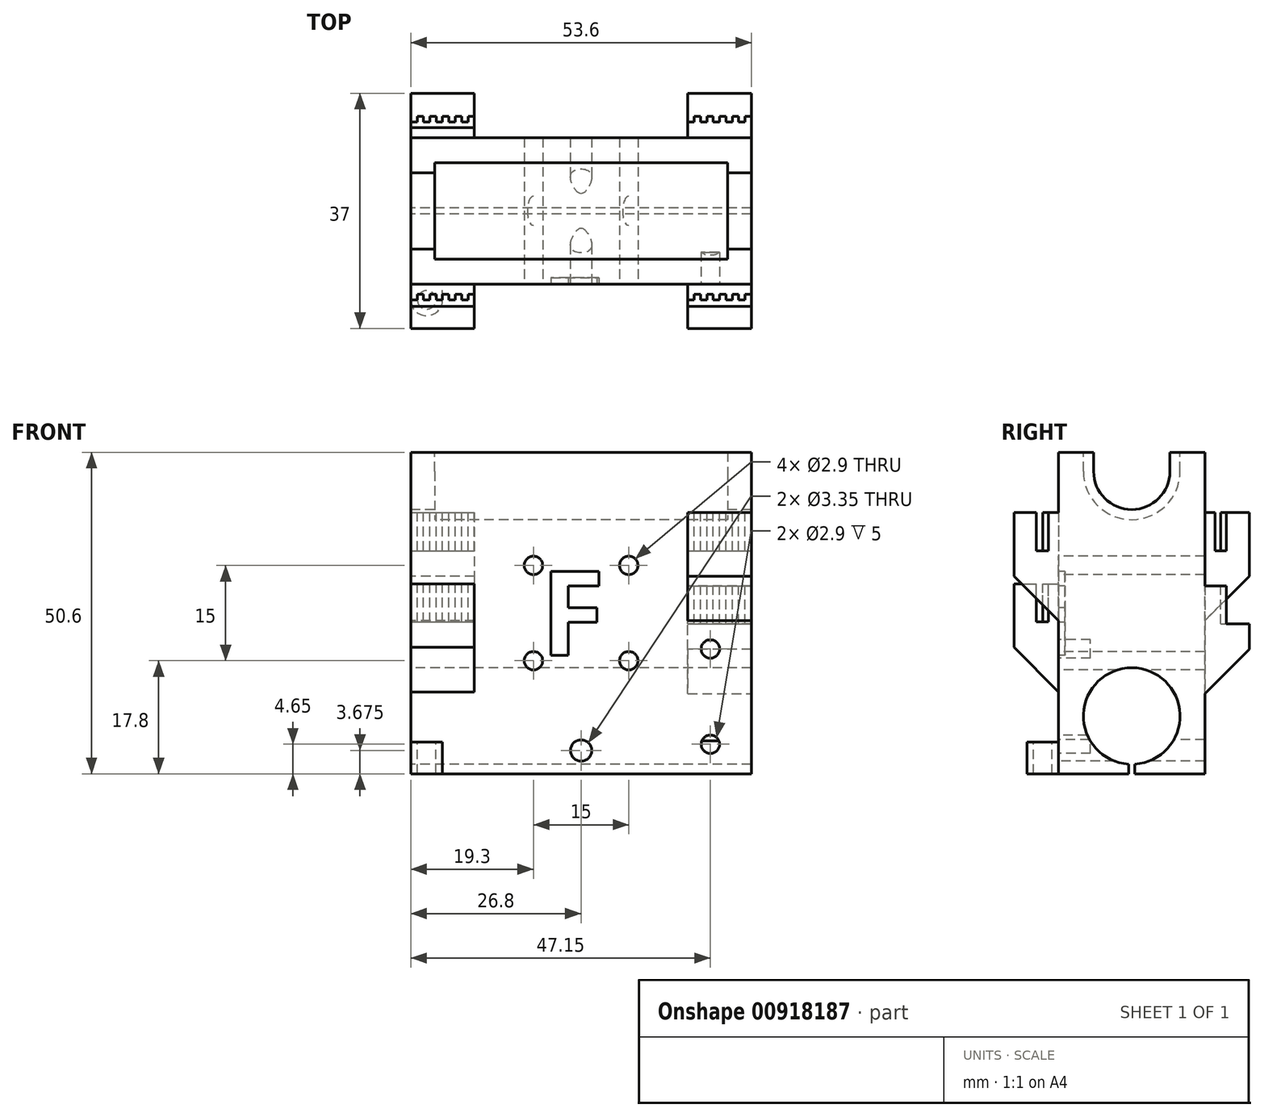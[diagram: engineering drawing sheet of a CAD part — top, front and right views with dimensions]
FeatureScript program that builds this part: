
annotation { "Feature Type Name" : "Feature", "Feature Type Description" : "" }
export const myFeature = defineFeature(function(context is Context, id is Id, definition is map)
    precondition{}
    {
        {
            assignVariable(context, id + "F0", {"name" : "LM8LUU", "anyValue" : 1.8});
        }
        {
            var Q0;
            Q0=qCreatedBy(makeId("Top.planeOp"),FACE);
            var sketch = newSketch(context, id + "F1", { "sketchPlane" : qUnion([Q0])});
            skLineSegment(sketch, "E0.bottom", {"start": v(0, 0) * mm, "end": v(53.6, 0) * mm});
            skLineSegment(sketch, "E0.top", {"start": v(0, 23) * mm, "end": v(53.6, 23) * mm});
            skLineSegment(sketch, "E0.left", {"start": v(0, 0) * mm, "end": v(0, 23) * mm});
            skLineSegment(sketch, "E0.right", {"start": v(53.6, 0) * mm, "end": v(53.6, 23) * mm});
            skSolve(sketch);
        }
        {
            var Q0;
            Q0=qSketchRegion(id+"F1",true);
            extrude(context, id + "F2", {"entities" : qUnion([Q0]), "depth" : 50.6 * mm});
        }
        {
            var Q0;
            Q0=makeQuery(id+"F2.opExtrude","SWEPT_FACE",FACE,{"disambiguationData":[OSD([sQuery(id+"F1.wireOp",EDGE,"E0.left")])]});
            var sketch = newSketch(context, id + "F3", { "sketchPlane" : qUnion([Q0])});
            skCircle(sketch, "E1", {"center": v(-11.5, 9.1) * mm, "radius": 7.6 * mm});
            skCircle(sketch, "E2", {"center": v(-11.5, 47.6) * mm, "radius": 6 * mm});
            skLineSegment(sketch, "E3", {"start": v(-23, 47.6) * mm, "end": v(0, 47.6) * mm, "construction": true});
            skLineSegment(sketch, "E4", {"start": v(-17.5, 50.6) * mm, "end": v(-17.5, 47.6) * mm});
            skLineSegment(sketch, "E5", {"start": v(-5.5, 50.6) * mm, "end": v(-5.5, 47.6) * mm});
            skLineSegment(sketch, "E6", {"start": v(-23, 9.1) * mm, "end": v(0, 9.1) * mm, "construction": true});
            skLineSegment(sketch, "E7", {"start": v(-11.5, 9.1) * mm, "end": v(-11.5, 0) * mm, "construction": true});
            skLineSegment(sketch, "E8", {"start": v(-11.5, 0) * mm, "end": v(-12, 0) * mm});
            skLineSegment(sketch, "E9", {"start": v(-12, 0) * mm, "end": v(-12, 1.52) * mm});
            skLineSegment(sketch, "E10", {"start": v(-12, 1.52) * mm, "end": v(-11, 1.52) * mm});
            skLineSegment(sketch, "E11", {"start": v(-11, 1.52) * mm, "end": v(-11, 0) * mm});
            skLineSegment(sketch, "E12", {"start": v(-11, 0) * mm, "end": v(-11.5, 0) * mm});
            skLineSegment(sketch, "E13", {"start": v(-11.5, 15.6) * mm, "end": v(-11.5, 16.7) * mm});
            skLineSegment(sketch, "E14", {"start": v(-11.5, 15.6) * mm, "end": v(-7, 15.22) * mm});
            skLineSegment(sketch, "E15", {"start": v(-11.5, 15.6) * mm, "end": v(-16, 15.22) * mm});
            skCircle(sketch, "E16", {"center": v(-11.5, 47.6) * mm, "radius": 7.6 * mm});
            skLineSegment(sketch, "E17", {"start": v(-3.9, 47.6) * mm, "end": v(-3.9, 50.6) * mm});
            skLineSegment(sketch, "E18", {"start": v(-19.1, 47.6) * mm, "end": v(-19.1, 50.6) * mm});
            skSolve(sketch);
        }
        {
            var Q0;
            {var subQ0=sQuery(id+"F3.wireOp",EDGE,"E14");var subQ1=sQuery(id+"F3.wireOp",EDGE,"E1");var subQ3=makeQuery(id+"F3.imprint","INTERSECT",VERTEX,{"disambiguationData":[OD(0.0)],"derivedFrom":[subQ1,subQ0]});Q0=makeQuery(id+"F3.imprint","IMPRINT",FACE,{"disambiguationData":[TD([[makeQuery(id+"F3.imprint","IMPRINT",EDGE,{"disambiguationData":[TD([[subQ3,-1.0]])],"derivedFrom":subQ1}),1.0]])]});}
            var Q1;
            {var subQ0=sQuery(id+"F3.wireOp",EDGE,"E15");var subQ1=sQuery(id+"F3.wireOp",EDGE,"E1");var subQ3=makeQuery(id+"F3.imprint","INTERSECT",VERTEX,{"disambiguationData":[OD(0.0)],"derivedFrom":[subQ1,subQ0]});Q1=makeQuery(id+"F3.imprint","IMPRINT",FACE,{"disambiguationData":[TD([[makeQuery(id+"F3.imprint","IMPRINT",EDGE,{"disambiguationData":[TD([[subQ3,1.0]])],"derivedFrom":subQ1}),1.0]])]});}
            var Q2;
            Q2=makeQuery(id+"F3.imprint","IMPRINT",FACE,{"disambiguationData":[TD([[makeQuery(id+"F3.imprint","IMPRINT",EDGE,{"derivedFrom":sQuery(id+"F3.wireOp",EDGE,"E8")}),-1.0]])]});
            var Q3;
            {var subQ0=sQuery(id+"F3.wireOp",EDGE,"E10");Q3=makeQuery(id+"F3.imprint","IMPRINT",FACE,{"disambiguationData":[TD([[makeQuery(id+"F3.imprint","IMPRINT",EDGE,{"derivedFrom":subQ0}),-1.0]])]});}
            var Q4;
            {var subQ3=sQuery(id+"F3.wireOp",EDGE,"E13");Q4=makeQuery(id+"F3.imprint","IMPRINT",FACE,{"disambiguationData":[TD([[makeQuery(id+"F3.imprint","IMPRINT",EDGE,{"derivedFrom":subQ3}),-1.0]])]});}
            var Q5;
            {var subQ3=sQuery(id+"F3.wireOp",EDGE,"E13");Q5=makeQuery(id+"F3.imprint","IMPRINT",FACE,{"disambiguationData":[TD([[makeQuery(id+"F3.imprint","IMPRINT",EDGE,{"derivedFrom":subQ3}),1.0]])]});}
            var Q6;
            {var subQ7=sQuery(id+"F3.wireOp",EDGE,"E10");Q6=makeQuery(id+"F3.imprint","IMPRINT",FACE,{"disambiguationData":[TD([[makeQuery(id+"F3.imprint","IMPRINT",EDGE,{"derivedFrom":subQ7}),1.0]])]});}
            var Q7;
            {var subQ3=sQuery(id+"F3.wireOp",EDGE,"E5");Q7=makeQuery(id+"F3.imprint","IMPRINT",FACE,{"disambiguationData":[TD([[makeQuery(id+"F3.imprint","IMPRINT",EDGE,{"derivedFrom":subQ3}),-1.0]])]});}
            var Q8;
            {var subQ0=sQuery(id+"F3.wireOp",EDGE,"E4");Q8=makeQuery(id+"F3.imprint","IMPRINT",FACE,{"disambiguationData":[TD([[makeQuery(id+"F3.imprint","IMPRINT",EDGE,{"derivedFrom":subQ0}),1.0]])]});}
            var Q9;
            {var subQ0=sQuery(id+"F3.wireOp",EDGE,"E4");Q9=makeQuery(id+"F3.imprint","IMPRINT",FACE,{"disambiguationData":[TD([[makeQuery(id+"F3.imprint","IMPRINT",EDGE,{"derivedFrom":subQ0}),1.0]])]});}
            var Q10;
            {var subQ3=sQuery(id+"F3.wireOp",EDGE,"E5");Q10=makeQuery(id+"F3.imprint","IMPRINT",FACE,{"disambiguationData":[TD([[makeQuery(id+"F3.imprint","IMPRINT",EDGE,{"derivedFrom":subQ3}),-1.0]])]});}
            var Q11;
            {var subQ1=sQuery(id+"F3.wireOp",EDGE,"E2");var subQ4=makeQuery(id+"F3.imprint","INTERSECT",VERTEX,{"derivedFrom":[subQ1,sQuery(id+"F3.wireOp",EDGE,"E5")]});Q11=makeQuery(id+"F3.imprint","IMPRINT",FACE,{"disambiguationData":[TD([[makeQuery(id+"F3.imprint","IMPRINT",EDGE,{"disambiguationData":[TD([[subQ4,-1.0]])],"derivedFrom":subQ1}),1.0]])]});}
            extrude(context, id + "F4", {"entities" : qUnion([Q0, Q1, Q2, Q3, Q4, Q5, Q6, Q7, Q8, Q9, Q10, Q11]), "operationType" : NewBodyOperationType.REMOVE, "endBound" : BoundingType.THROUGH_ALL, "oppositeDirection" : true, "depth" : 25 * mm});
        }
        {
            var Q0;
            {var subQ3=sQuery(id+"F3.wireOp",EDGE,"E4");Q0=makeQuery(id+"F3.imprint","IMPRINT",FACE,{"disambiguationData":[TD([[makeQuery(id+"F3.imprint","IMPRINT",EDGE,{"derivedFrom":subQ3}),-1.0]])]});}
            var Q1;
            {var subQ3=sQuery(id+"F3.wireOp",EDGE,"E18");Q1=makeQuery(id+"F3.imprint","IMPRINT",FACE,{"disambiguationData":[TD([[makeQuery(id+"F3.imprint","IMPRINT",EDGE,{"derivedFrom":subQ3}),-1.0]])]});}
            var Q2;
            {var subQ3=sQuery(id+"F3.wireOp",EDGE,"E17");Q2=makeQuery(id+"F3.imprint","IMPRINT",FACE,{"disambiguationData":[TD([[makeQuery(id+"F3.imprint","IMPRINT",EDGE,{"derivedFrom":subQ3}),1.0]])]});}
            extrude(context, id + "F5", {"entities" : qUnion([Q0, Q1, Q2]), "operationType" : NewBodyOperationType.REMOVE, "oppositeDirection" : true, "depth" : (46.25 + getVariable(context, 'LM8LUU') * 2) * mm});
        }
        {
            var Q0;
            {var subQ3=sQuery(id+"F3.wireOp",EDGE,"E4");Q0=makeQuery(id+"F3.imprint","IMPRINT",FACE,{"disambiguationData":[TD([[makeQuery(id+"F3.imprint","IMPRINT",EDGE,{"derivedFrom":subQ3}),-1.0]])]});}
            var Q1;
            {var subQ3=sQuery(id+"F3.wireOp",EDGE,"E18");Q1=makeQuery(id+"F3.imprint","IMPRINT",FACE,{"disambiguationData":[TD([[makeQuery(id+"F3.imprint","IMPRINT",EDGE,{"derivedFrom":subQ3}),-1.0]])]});}
            var Q2;
            {var subQ3=sQuery(id+"F3.wireOp",EDGE,"E17");Q2=makeQuery(id+"F3.imprint","IMPRINT",FACE,{"disambiguationData":[TD([[makeQuery(id+"F3.imprint","IMPRINT",EDGE,{"derivedFrom":subQ3}),1.0]])]});}
            extrude(context, id + "F6", {"entities" : qUnion([Q0, Q1, Q2]), "operationType" : NewBodyOperationType.ADD, "oppositeDirection" : true, "depth" : (26.75 - getVariable(context, 'LM8LUU')) * mm});
        }
        {
            var Q0;
            {var subQ3=sQuery(id+"F3.wireOp",EDGE,"E4");Q0=makeQuery(id+"F3.imprint","IMPRINT",FACE,{"disambiguationData":[TD([[makeQuery(id+"F3.imprint","IMPRINT",EDGE,{"derivedFrom":subQ3}),-1.0]])]});}
            var Q1;
            {var subQ3=sQuery(id+"F3.wireOp",EDGE,"E18");Q1=makeQuery(id+"F3.imprint","IMPRINT",FACE,{"disambiguationData":[TD([[makeQuery(id+"F3.imprint","IMPRINT",EDGE,{"derivedFrom":subQ3}),-1.0]])]});}
            var Q2;
            {var subQ3=sQuery(id+"F3.wireOp",EDGE,"E17");Q2=makeQuery(id+"F3.imprint","IMPRINT",FACE,{"disambiguationData":[TD([[makeQuery(id+"F3.imprint","IMPRINT",EDGE,{"derivedFrom":subQ3}),1.0]])]});}
            extrude(context, id + "F7", {"entities" : qUnion([Q0, Q1, Q2]), "operationType" : NewBodyOperationType.REMOVE, "oppositeDirection" : true, "depth" : (23.25 + getVariable(context, 'LM8LUU')) * mm});
        }
        {
            var Q0;
            {var subQ3=sQuery(id+"F3.wireOp",EDGE,"E4");Q0=makeQuery(id+"F3.imprint","IMPRINT",FACE,{"disambiguationData":[TD([[makeQuery(id+"F3.imprint","IMPRINT",EDGE,{"derivedFrom":subQ3}),-1.0]])]});}
            var Q1;
            {var subQ3=sQuery(id+"F3.wireOp",EDGE,"E18");Q1=makeQuery(id+"F3.imprint","IMPRINT",FACE,{"disambiguationData":[TD([[makeQuery(id+"F3.imprint","IMPRINT",EDGE,{"derivedFrom":subQ3}),-1.0]])]});}
            var Q2;
            {var subQ3=sQuery(id+"F3.wireOp",EDGE,"E17");Q2=makeQuery(id+"F3.imprint","IMPRINT",FACE,{"disambiguationData":[TD([[makeQuery(id+"F3.imprint","IMPRINT",EDGE,{"derivedFrom":subQ3}),1.0]])]});}
            extrude(context, id + "F8", {"entities" : qUnion([Q0, Q1, Q2]), "operationType" : NewBodyOperationType.ADD, "oppositeDirection" : true, "depth" : 3.75 * mm});
        }
        {
            var Q0;
            Q0=makeQuery(id+"F2.opExtrude","SWEPT_FACE",FACE,{"disambiguationData":[OSD([sQuery(id+"F1.wireOp",EDGE,"E0.bottom")])]});
            var sketch = newSketch(context, id + "F9", { "sketchPlane" : qUnion([Q0])});
            skLineSegment(sketch, "E19.bottom", {"start": v(0, 29.9) * mm, "end": v(10, 29.9) * mm});
            skLineSegment(sketch, "E19.top", {"start": v(0, 9.9) * mm, "end": v(10, 9.9) * mm});
            skLineSegment(sketch, "E19.left", {"start": v(0, 29.9) * mm, "end": v(0, 9.9) * mm});
            skLineSegment(sketch, "E19.right", {"start": v(10, 29.9) * mm, "end": v(10, 9.9) * mm});
            skLineSegment(sketch, "E20.bottom", {"start": v(53.6, 41.1) * mm, "end": v(43.6, 41.1) * mm});
            skLineSegment(sketch, "E20.top", {"start": v(53.6, 21.1) * mm, "end": v(43.6, 21.1) * mm});
            skLineSegment(sketch, "E20.left", {"start": v(53.6, 41.1) * mm, "end": v(53.6, 21.1) * mm});
            skLineSegment(sketch, "E20.right", {"start": v(43.6, 41.1) * mm, "end": v(43.6, 21.1) * mm});
            skPoint(sketch, "E21", {"position": v(0, 47.6) * mm});
            skPoint(sketch, "E22", {"position": v(0, 9.4) * mm});
            skSolve(sketch);
        }
        {
            var Q0;
            Q0=qSketchRegion(id+"F9",true);
            extrude(context, id + "F10", {"entities" : qUnion([Q0]), "operationType" : NewBodyOperationType.ADD, "depth" : 7 * mm});
        }
        {
            var Q0;
            Q0=makeQuery(id+"F10.opExtrude","CAP_EDGE",EDGE,{"disambiguationData":[OSD([sQuery(id+"F9.wireOp",EDGE,"E19.top")])],"isStart":false});
            var Q1;
            Q1=makeQuery(id+"F10.opExtrude","CAP_EDGE",EDGE,{"disambiguationData":[OSD([sQuery(id+"F9.wireOp",EDGE,"E20.top")])],"isStart":false});
            chamfer(context, id + "F11", {"entities" : qUnion([Q0, Q1]), "width" : 10 * mm, "tangentPropagation" : true});
        }
        {
            var Q0;
            Q0=makeQuery(id+"F10.opExtrude","SWEPT_FACE",FACE,{"disambiguationData":[OSD([sQuery(id+"F9.wireOp",EDGE,"E19.bottom")])]});
            var sketch = newSketch(context, id + "F12", { "sketchPlane" : qUnion([Q0])});
            skLineSegment(sketch, "E23", {"start": v(-935.9, 0) * mm, "end": v(-935.88, -4.54) * mm});
            skLineSegment(sketch, "E24.left", {"start": v(0, -3.5) * mm, "end": v(0, -1.6) * mm});
            skLineSegment(sketch, "E25", {"start": v(6, -2.5) * mm, "end": v(7, -2.5) * mm});
            skLineSegment(sketch, "E26", {"start": v(4, -2.5) * mm, "end": v(5, -2.5) * mm});
            skLineSegment(sketch, "E27", {"start": v(0, -2.5) * mm, "end": v(1, -2.5) * mm});
            skLineSegment(sketch, "E28", {"start": v(7, -1.6) * mm, "end": v(8, -1.6) * mm});
            skLineSegment(sketch, "E29", {"start": v(2, -2.5) * mm, "end": v(3, -2.5) * mm});
            skLineSegment(sketch, "E30", {"start": v(3, -1.6) * mm, "end": v(4, -1.6) * mm});
            skLineSegment(sketch, "E31", {"start": v(8, -2.5) * mm, "end": v(9, -2.5) * mm});
            skLineSegment(sketch, "E32", {"start": v(8, -1.6) * mm, "end": v(8, -2.5) * mm});
            skLineSegment(sketch, "E33", {"start": v(9, -2.5) * mm, "end": v(9, -1.6) * mm});
            skLineSegment(sketch, "E34", {"start": v(10, -1.6) * mm, "end": v(10, -2.5) * mm});
            skLineSegment(sketch, "E35", {"start": v(6, -1.6) * mm, "end": v(6, -2.5) * mm});
            skLineSegment(sketch, "E36", {"start": v(2, -1.6) * mm, "end": v(2, -2.5) * mm});
            skLineSegment(sketch, "E37", {"start": v(1, -1.6) * mm, "end": v(2, -1.6) * mm});
            skLineSegment(sketch, "E38", {"start": v(1, -2.5) * mm, "end": v(1, -1.6) * mm});
            skLineSegment(sketch, "E39", {"start": v(9, -1.6) * mm, "end": v(10, -1.6) * mm});
            skLineSegment(sketch, "E40", {"start": v(5, -1.6) * mm, "end": v(6, -1.6) * mm});
            skLineSegment(sketch, "E41", {"start": v(5, -2.5) * mm, "end": v(5, -1.6) * mm});
            skLineSegment(sketch, "E42", {"start": v(3, -2.5) * mm, "end": v(3, -1.6) * mm});
            skLineSegment(sketch, "E43", {"start": v(4, -1.6) * mm, "end": v(4, -2.5) * mm});
            skLineSegment(sketch, "E44", {"start": v(7, -2.5) * mm, "end": v(7, -1.6) * mm});
            skLineSegment(sketch, "E45", {"start": v(0, -1.6) * mm, "end": v(0, -2.5) * mm});
            skLineSegment(sketch, "E46", {"start": v(10, -2.5) * mm, "end": v(10, -3.5) * mm});
            skLineSegment(sketch, "E47", {"start": v(0, -3.5) * mm, "end": v(10, -3.5) * mm});
            skLineSegment(sketch, "E48", {"start": v(5.3, -1.6) * mm, "end": v(5.3, 0) * mm});
            skSolve(sketch);
        }
        {
            var Q0;
            Q0=qSketchRegion(id+"F12",true);
            extrude(context, id + "F13", {"entities" : qUnion([Q0]), "operationType" : NewBodyOperationType.REMOVE, "oppositeDirection" : true, "depth" : 6 * mm});
        }
        {
            var Q0;
            Q0=makeQuery(id+"F10.opExtrude","SWEPT_FACE",FACE,{"disambiguationData":[OSD([sQuery(id+"F9.wireOp",EDGE,"E20.bottom")])]});
            var sketch = newSketch(context, id + "F14", { "sketchPlane" : qUnion([Q0])});
            skLineSegment(sketch, "E49.left", {"start": v(43.6, -3.5) * mm, "end": v(43.6, -1.6) * mm});
            skLineSegment(sketch, "E50", {"start": v(49.6, -2.5) * mm, "end": v(50.6, -2.5) * mm});
            skLineSegment(sketch, "E51", {"start": v(47.6, -2.5) * mm, "end": v(48.6, -2.5) * mm});
            skLineSegment(sketch, "E52", {"start": v(43.6, -2.5) * mm, "end": v(44.6, -2.5) * mm});
            skLineSegment(sketch, "E53", {"start": v(50.6, -1.6) * mm, "end": v(51.6, -1.6) * mm});
            skLineSegment(sketch, "E54", {"start": v(45.6, -2.5) * mm, "end": v(46.6, -2.5) * mm});
            skLineSegment(sketch, "E55", {"start": v(46.6, -1.6) * mm, "end": v(47.6, -1.6) * mm});
            skLineSegment(sketch, "E56", {"start": v(51.6, -2.5) * mm, "end": v(52.6, -2.5) * mm});
            skLineSegment(sketch, "E57", {"start": v(51.6, -1.6) * mm, "end": v(51.6, -2.5) * mm});
            skLineSegment(sketch, "E58", {"start": v(52.6, -2.5) * mm, "end": v(52.6, -1.6) * mm});
            skLineSegment(sketch, "E59", {"start": v(53.6, -1.6) * mm, "end": v(53.6, -2.5) * mm});
            skLineSegment(sketch, "E60", {"start": v(49.6, -1.6) * mm, "end": v(49.6, -2.5) * mm});
            skLineSegment(sketch, "E61", {"start": v(45.6, -1.6) * mm, "end": v(45.6, -2.5) * mm});
            skLineSegment(sketch, "E62", {"start": v(44.6, -1.6) * mm, "end": v(45.6, -1.6) * mm});
            skLineSegment(sketch, "E63", {"start": v(44.6, -2.5) * mm, "end": v(44.6, -1.6) * mm});
            skLineSegment(sketch, "E64", {"start": v(52.6, -1.6) * mm, "end": v(53.6, -1.6) * mm});
            skLineSegment(sketch, "E65", {"start": v(48.6, -1.6) * mm, "end": v(49.6, -1.6) * mm});
            skLineSegment(sketch, "E66", {"start": v(48.6, -2.5) * mm, "end": v(48.6, -1.6) * mm});
            skLineSegment(sketch, "E67", {"start": v(46.6, -2.5) * mm, "end": v(46.6, -1.6) * mm});
            skLineSegment(sketch, "E68", {"start": v(47.6, -1.6) * mm, "end": v(47.6, -2.5) * mm});
            skLineSegment(sketch, "E69", {"start": v(50.6, -2.5) * mm, "end": v(50.6, -1.6) * mm});
            skLineSegment(sketch, "E70", {"start": v(43.6, -1.6) * mm, "end": v(43.6, -2.5) * mm});
            skLineSegment(sketch, "E71", {"start": v(53.6, -2.5) * mm, "end": v(53.6, -3.5) * mm});
            skLineSegment(sketch, "E72", {"start": v(43.6, -3.5) * mm, "end": v(53.6, -3.5) * mm});
            skLineSegment(sketch, "E73", {"start": v(48.83, -1.6) * mm, "end": v(48.83, 0) * mm});
            skSolve(sketch);
        }
        {
            var Q0;
            Q0=qSketchRegion(id+"F14",true);
            extrude(context, id + "F15", {"entities" : qUnion([Q0]), "operationType" : NewBodyOperationType.REMOVE, "oppositeDirection" : true, "depth" : 6 * mm});
        }
        {
            var Q0;
            Q0=makeQuery(id+"F2.opExtrude","SWEPT_FACE",FACE,{"disambiguationData":[OSD([sQuery(id+"F1.wireOp",EDGE,"E0.top")])]});
            var sketch = newSketch(context, id + "F16", { "sketchPlane" : qUnion([Q0])});
            skLineSegment(sketch, "E74.bottom", {"start": v(-53.6, 9.6) * mm, "end": v(-43.6, 9.6) * mm});
            skLineSegment(sketch, "E74.top", {"start": v(-53.6, 29.6) * mm, "end": v(-43.6, 29.6) * mm});
            skLineSegment(sketch, "E74.left", {"start": v(-53.6, 9.6) * mm, "end": v(-53.6, 29.6) * mm});
            skLineSegment(sketch, "E74.right", {"start": v(-43.6, 9.6) * mm, "end": v(-43.6, 29.6) * mm});
            skLineSegment(sketch, "E75.bottom", {"start": v(0, 41.1) * mm, "end": v(-10, 41.1) * mm});
            skLineSegment(sketch, "E75.top", {"start": v(0, 21.1) * mm, "end": v(-10, 21.1) * mm});
            skLineSegment(sketch, "E75.left", {"start": v(0, 41.1) * mm, "end": v(0, 21.1) * mm});
            skLineSegment(sketch, "E75.right", {"start": v(-10, 41.1) * mm, "end": v(-10, 21.1) * mm});
            skSolve(sketch);
        }
        {
            var Q0;
            Q0=qSketchRegion(id+"F16",true);
            extrude(context, id + "F17", {"entities" : qUnion([Q0]), "operationType" : NewBodyOperationType.ADD, "depth" : 7 * mm});
        }
        {
            var Q0;
            Q0=makeQuery(id+"F17.opExtrude","SWEPT_FACE",FACE,{"disambiguationData":[OSD([sQuery(id+"F16.wireOp",EDGE,"E74.top")])]});
            var sketch = newSketch(context, id + "F18", { "sketchPlane" : qUnion([Q0])});
            skLineSegment(sketch, "E76.left", {"start": v(43.6, 24.6) * mm, "end": v(43.6, 26.4) * mm});
            skLineSegment(sketch, "E77", {"start": v(49.6, 25.5) * mm, "end": v(50.6, 25.5) * mm});
            skLineSegment(sketch, "E78", {"start": v(47.6, 25.5) * mm, "end": v(48.6, 25.5) * mm});
            skLineSegment(sketch, "E79", {"start": v(43.6, 25.5) * mm, "end": v(44.6, 25.5) * mm});
            skLineSegment(sketch, "E80", {"start": v(50.6, 26.4) * mm, "end": v(51.6, 26.4) * mm});
            skLineSegment(sketch, "E81", {"start": v(45.6, 25.5) * mm, "end": v(46.6, 25.5) * mm});
            skLineSegment(sketch, "E82", {"start": v(46.6, 26.4) * mm, "end": v(47.6, 26.4) * mm});
            skLineSegment(sketch, "E83", {"start": v(51.6, 25.5) * mm, "end": v(52.6, 25.5) * mm});
            skLineSegment(sketch, "E84", {"start": v(51.6, 26.4) * mm, "end": v(51.6, 25.5) * mm});
            skLineSegment(sketch, "E85", {"start": v(52.6, 25.5) * mm, "end": v(52.6, 26.4) * mm});
            skLineSegment(sketch, "E86", {"start": v(53.6, 26.4) * mm, "end": v(53.6, 25.5) * mm});
            skLineSegment(sketch, "E87", {"start": v(49.6, 26.4) * mm, "end": v(49.6, 25.5) * mm});
            skLineSegment(sketch, "E88", {"start": v(45.6, 26.4) * mm, "end": v(45.6, 25.5) * mm});
            skLineSegment(sketch, "E89", {"start": v(44.6, 26.4) * mm, "end": v(45.6, 26.4) * mm});
            skLineSegment(sketch, "E90", {"start": v(44.6, 25.5) * mm, "end": v(44.6, 26.4) * mm});
            skLineSegment(sketch, "E91", {"start": v(52.6, 26.4) * mm, "end": v(53.6, 26.4) * mm});
            skLineSegment(sketch, "E92", {"start": v(48.6, 26.4) * mm, "end": v(49.6, 26.4) * mm});
            skLineSegment(sketch, "E93", {"start": v(48.6, 25.5) * mm, "end": v(48.6, 26.4) * mm});
            skLineSegment(sketch, "E94", {"start": v(46.6, 25.5) * mm, "end": v(46.6, 26.4) * mm});
            skLineSegment(sketch, "E95", {"start": v(47.6, 26.4) * mm, "end": v(47.6, 25.5) * mm});
            skLineSegment(sketch, "E96", {"start": v(50.6, 25.5) * mm, "end": v(50.6, 26.4) * mm});
            skLineSegment(sketch, "E97", {"start": v(43.6, 26.4) * mm, "end": v(43.6, 25.5) * mm});
            skLineSegment(sketch, "E98", {"start": v(53.6, 25.5) * mm, "end": v(53.6, 24.6) * mm});
            skLineSegment(sketch, "E99", {"start": v(43.6, 24.6) * mm, "end": v(53.6, 24.6) * mm});
            skLineSegment(sketch, "E100", {"start": v(48.6, 24.6) * mm, "end": v(48.6, 23) * mm});
            skSolve(sketch);
        }
        {
            var Q0;
            {var subQ4=sQuery(id+"F18.wireOp",EDGE,"E76.left");Q0=makeQuery(id+"F18.imprint","IMPRINT",FACE,{"disambiguationData":[TD([[makeQuery(id+"F18.imprint","IMPRINT",EDGE,{"derivedFrom":subQ4}),1.0]])]});}
            extrude(context, id + "F19", {"entities" : qUnion([Q0]), "operationType" : NewBodyOperationType.REMOVE, "oppositeDirection" : true, "depth" : 6 * mm});
        }
        {
            var Q0;
            Q0=makeQuery(id+"F17.opExtrude","SWEPT_FACE",FACE,{"disambiguationData":[OSD([sQuery(id+"F16.wireOp",EDGE,"E75.bottom")])]});
            var sketch = newSketch(context, id + "F20", { "sketchPlane" : qUnion([Q0])});
            skLineSegment(sketch, "E101", {"start": v(6, 25.5) * mm, "end": v(7, 25.5) * mm});
            skLineSegment(sketch, "E102", {"start": v(4, 25.5) * mm, "end": v(5, 25.5) * mm});
            skLineSegment(sketch, "E103", {"start": v(0, 25.5) * mm, "end": v(1, 25.5) * mm});
            skLineSegment(sketch, "E104", {"start": v(7, 26.4) * mm, "end": v(8, 26.4) * mm});
            skLineSegment(sketch, "E105", {"start": v(2, 25.5) * mm, "end": v(3, 25.5) * mm});
            skLineSegment(sketch, "E106", {"start": v(3, 26.4) * mm, "end": v(4, 26.4) * mm});
            skLineSegment(sketch, "E107", {"start": v(8, 25.5) * mm, "end": v(9, 25.5) * mm});
            skLineSegment(sketch, "E108", {"start": v(8, 26.4) * mm, "end": v(8, 25.5) * mm});
            skLineSegment(sketch, "E109", {"start": v(9, 25.5) * mm, "end": v(9, 26.4) * mm});
            skLineSegment(sketch, "E110", {"start": v(10, 26.4) * mm, "end": v(10, 25.5) * mm});
            skLineSegment(sketch, "E111", {"start": v(6, 26.4) * mm, "end": v(6, 25.5) * mm});
            skLineSegment(sketch, "E112", {"start": v(2, 26.4) * mm, "end": v(2, 25.5) * mm});
            skLineSegment(sketch, "E113", {"start": v(1, 26.4) * mm, "end": v(2, 26.4) * mm});
            skLineSegment(sketch, "E114", {"start": v(1, 25.5) * mm, "end": v(1, 26.4) * mm});
            skLineSegment(sketch, "E115", {"start": v(9, 26.4) * mm, "end": v(10, 26.4) * mm});
            skLineSegment(sketch, "E116", {"start": v(5, 26.4) * mm, "end": v(6, 26.4) * mm});
            skLineSegment(sketch, "E117", {"start": v(5, 25.5) * mm, "end": v(5, 26.4) * mm});
            skLineSegment(sketch, "E118", {"start": v(3, 25.5) * mm, "end": v(3, 26.4) * mm});
            skLineSegment(sketch, "E119", {"start": v(4, 26.4) * mm, "end": v(4, 25.5) * mm});
            skLineSegment(sketch, "E120", {"start": v(7, 25.5) * mm, "end": v(7, 26.4) * mm});
            skLineSegment(sketch, "E121", {"start": v(10, 25.5) * mm, "end": v(10, 24.6) * mm});
            skLineSegment(sketch, "E122", {"start": v(0, 24.6) * mm, "end": v(10, 24.6) * mm});
            skLineSegment(sketch, "E123", {"start": v(5, 24.6) * mm, "end": v(5, 23) * mm});
            skLineSegment(sketch, "E124", {"start": v(0, 24.6) * mm, "end": v(0, 25.5) * mm});
            skSolve(sketch);
        }
        {
            var Q0;
            Q0=makeQuery(id+"F20.imprint","IMPRINT",FACE,{"disambiguationData":[TD([[makeQuery(id+"F20.imprint","IMPRINT",EDGE,{"derivedFrom":sQuery(id+"F20.wireOp",EDGE,"E101")}),-1.0]])]});
            extrude(context, id + "F21", {"entities" : qUnion([Q0]), "operationType" : NewBodyOperationType.REMOVE, "oppositeDirection" : true, "depth" : 6 * mm});
        }
        {
            var Q0;
            Q0=makeQuery(id+"F17.opExtrude","CAP_EDGE",EDGE,{"disambiguationData":[OSD([sQuery(id+"F16.wireOp",EDGE,"E75.top")])],"isStart":false});
            var Q1;
            Q1=makeQuery(id+"F17.opExtrude","CAP_EDGE",EDGE,{"disambiguationData":[OSD([sQuery(id+"F16.wireOp",EDGE,"E74.bottom")])],"isStart":false});
            chamfer(context, id + "F22", {"entities" : qUnion([Q0, Q1]), "width" : 10 * mm, "tangentPropagation" : true});
        }
        {
            var Q0;
            Q0=makeQuery(id+"F2.opExtrude","SWEPT_FACE",FACE,{"disambiguationData":[OSD([sQuery(id+"F1.wireOp",EDGE,"E0.bottom")])]});
            var sketch = newSketch(context, id + "F23", { "sketchPlane" : qUnion([Q0])});
            skCircle(sketch, "E125", {"center": v(19.3, 32.8) * mm, "radius": 1.45 * mm});
            skCircle(sketch, "E126", {"center": v(34.3, 32.8) * mm, "radius": 1.45 * mm});
            skCircle(sketch, "E127", {"center": v(19.3, 17.8) * mm, "radius": 1.45 * mm});
            skCircle(sketch, "E128", {"center": v(34.3, 17.8) * mm, "radius": 1.45 * mm});
            skLineSegment(sketch, "E129", {"start": v(19.3, 32.8) * mm, "end": v(0, 32.8) * mm});
            skLineSegment(sketch, "E130", {"start": v(34.3, 17.8) * mm, "end": v(53.6, 17.8) * mm});
            skLineSegment(sketch, "E131", {"start": v(34.3, 32.8) * mm, "end": v(34.3, 50.6) * mm});
            skLineSegment(sketch, "E132", {"start": v(19.3, 17.8) * mm, "end": v(19.3, 0) * mm});
            skCircle(sketch, "E133", {"center": v(26.8, 3.68) * mm, "radius": 1.68 * mm});
            skLineSegment(sketch, "E134", {"start": v(26.8, 0) * mm, "end": v(26.8, 13.82) * mm, "construction": true});
            skSolve(sketch);
        }
        {
            var Q0;
            Q0=qSketchRegion(id+"F23",true);
            var Q1;
            Q1=makeQuery(id+"F23.imprint","IMPRINT",FACE,{"disambiguationData":[TD([[makeQuery(id+"F23.imprint","IMPRINT",EDGE,{"derivedFrom":sQuery(id+"F23.wireOp",EDGE,"E125")}),1.0]])]});
            var Q2;
            Q2=makeQuery(id+"F23.imprint","IMPRINT",FACE,{"disambiguationData":[TD([[makeQuery(id+"F23.imprint","IMPRINT",EDGE,{"derivedFrom":sQuery(id+"F23.wireOp",EDGE,"E126")}),1.0]])]});
            var Q3;
            Q3=makeQuery(id+"F23.imprint","IMPRINT",FACE,{"disambiguationData":[TD([[makeQuery(id+"F23.imprint","IMPRINT",EDGE,{"derivedFrom":sQuery(id+"F23.wireOp",EDGE,"E128")}),1.0]])]});
            var Q4;
            Q4=makeQuery(id+"F23.imprint","IMPRINT",FACE,{"disambiguationData":[TD([[makeQuery(id+"F23.imprint","IMPRINT",EDGE,{"derivedFrom":sQuery(id+"F23.wireOp",EDGE,"E127")}),1.0]])]});
            extrude(context, id + "F24", {"entities" : qUnion([Q0, Q1, Q2, Q3, Q4]), "operationType" : NewBodyOperationType.REMOVE, "flatOperationType" : FlatOperationType.REMOVE, "endBound" : BoundingType.THROUGH_ALL, "oppositeDirection" : true, "depth" : 25 * mm, "offsetDistance" : 25 * mm, "domain" : OperationDomain.MODEL});
        }
        {
            var Q0;
            Q0=makeQuery(id+"F2.opExtrude","SWEPT_FACE",FACE,{"disambiguationData":[OSD([sQuery(id+"F1.wireOp",EDGE,"E0.bottom")])]});
            var sketch = newSketch(context, id + "F25", { "sketchPlane" : qUnion([Q0])});
            skCircle(sketch, "E135", {"center": v(47.15, 19.65) * mm, "radius": 1.45 * mm});
            skCircle(sketch, "E136", {"center": v(47.15, 4.65) * mm, "radius": 1.45 * mm});
            skSolve(sketch);
        }
        {
            var Q0;
            Q0=qSketchRegion(id+"F25",true);
            extrude(context, id + "F26", {"entities" : qUnion([Q0]), "operationType" : NewBodyOperationType.REMOVE, "oppositeDirection" : true, "depth" : 5 * mm});
        }
        {
            var Q0;
            Q0=makeQuery(id+"F2.opExtrude","SWEPT_FACE",FACE,{"disambiguationData":[OSD([sQuery(id+"F1.wireOp",EDGE,"E0.bottom")])]});
            var sketch = newSketch(context, id + "F27", { "sketchPlane" : qUnion([Q0])});
            skText(sketch, "E137", { "text": "F", "fontName": "OpenSans-Bold.ttf"});
            skLineSegment(sketch, "E138", {"start": v(19.3, 32.8) * mm, "end": v(19.3, 17.8) * mm, "construction": true});
            skLineSegment(sketch, "E139", {"start": v(19.3, 17.8) * mm, "end": v(34.3, 17.8) * mm, "construction": true});
            skLineSegment(sketch, "E140", {"start": v(34.3, 17.8) * mm, "end": v(34.3, 32.8) * mm, "construction": true});
            skLineSegment(sketch, "E141", {"start": v(34.3, 32.8) * mm, "end": v(19.3, 32.8) * mm, "construction": true});
            skLineSegment(sketch, "E142", {"start": v(19.3, 25.3) * mm, "end": v(22.2, 25.3) * mm, "construction": true});
            skLineSegment(sketch, "E143", {"start": v(31.4, 25.3) * mm, "end": v(34.3, 25.3) * mm, "construction": true});
            skLineSegment(sketch, "E144", {"start": v(26.8, 18.66) * mm, "end": v(26.8, 17.8) * mm, "construction": true});
            skLineSegment(sketch, "E145", {"start": v(26.8, 32.8) * mm, "end": v(26.8, 31.94) * mm, "construction": true});
            const initialGuessF27  = {"E137": [0.0204, 0.01866, 1, 0, 0.01328]};
            skSetInitialGuess(sketch, initialGuessF27);
            skSolve(sketch);
        }
        {
            var Q0;
            Q0=qSketchRegion(id+"F27",true);
            extrude(context, id + "F28", {"entities" : qUnion([Q0]), "operationType" : NewBodyOperationType.REMOVE, "oppositeDirection" : true, "depth" : 1 * mm});
        }
        {
            var Q0;
            Q0=makeQuery(id+"F2.opExtrude","SWEPT_FACE",FACE,{"disambiguationData":[OSD([sQuery(id+"F1.wireOp",EDGE,"E0.bottom")])]});
            var sketch = newSketch(context, id + "F29", { "sketchPlane" : qUnion([Q0])});
            skLineSegment(sketch, "E146.bottom", {"start": v(0, 0) * mm, "end": v(5, 0) * mm});
            skLineSegment(sketch, "E146.top", {"start": v(0, 5) * mm, "end": v(5, 5) * mm});
            skLineSegment(sketch, "E146.left", {"start": v(0, 0) * mm, "end": v(0, 5) * mm});
            skLineSegment(sketch, "E146.right", {"start": v(5, 0) * mm, "end": v(5, 5) * mm});
            skSolve(sketch);
        }
        {
            var Q0;
            Q0=qSketchRegion(id+"F29",true);
            extrude(context, id + "F30", {"entities" : qUnion([Q0]), "operationType" : NewBodyOperationType.ADD, "depth" : 5 * mm});
        }
        {
            var Q0;
            Q0=makeQuery(id+"F30.opExtrude","SWEPT_FACE",FACE,{"disambiguationData":[OSD([sQuery(id+"F29.wireOp",EDGE,"E146.top")])]});
            var sketch = newSketch(context, id + "F31", { "sketchPlane" : qUnion([Q0])});
            skCircle(sketch, "E147", {"center": v(2.5, -2.5) * mm, "radius": 1.45 * mm});
            skLineSegment(sketch, "E148", {"start": v(0, -2.5) * mm, "end": v(5, -2.5) * mm});
            skSolve(sketch);
        }
        {
            var Q0;
            Q0=qSketchRegion(id+"F31",true);
            extrude(context, id + "F32", {"entities" : qUnion([Q0]), "operationType" : NewBodyOperationType.REMOVE, "oppositeDirection" : true, "depth" : 25 * mm});
        }
        {
            var Q0;
            Q0=makeQuery(id+"F30.opExtrude","CAP_EDGE",EDGE,{"disambiguationData":[OSD([sQuery(id+"F29.wireOp",EDGE,"E146.left")])],"isStart":false});
            var Q1;
            Q1=makeQuery(id+"F30.opExtrude","CAP_EDGE",EDGE,{"disambiguationData":[OSD([sQuery(id+"F29.wireOp",EDGE,"E146.right")])],"isStart":false});
            fillet(context, id + "F33", {"entities" : qUnion([Q0, Q1]), "radius" : 2.5 * mm, "tangentPropagation" : true, "allowEdgeOverflow" : false});
        }
    });
